FCSTD DOCUMENT  (FreeCAD 0.19R)
Label: aileron_right_assembly
License: All rights reserved
LicenseURL: http://en.wikipedia.org/wiki/All_rights_reserved
objects: App::Link×3, App::DocumentObjectGroup×2, PartDesign::CoordinateSystem×1, App::FeaturePython×1, App::Part×1
note: 1 computed .brp shape members not serialized (recipe doc carries the construction recipe); baked Part::Feature solids carry a one-line shape summary decoded from their .brp
EXTERNAL_REF file=aileron_right_part.FCStd obj=LCS_Origin
EXTERNAL_REF file=aileron_right_part.FCStd obj=Model
EXTERNAL_REF file=aileron_right_part.FCStd obj=LCS_2
EXTERNAL_REF file=attach_aileron_part.FCStd obj=LCS_1
EXTERNAL_REF file=attach_aileron_part.FCStd obj=Model
EXTERNAL_REF file=aileron_right_part.FCStd obj=LCS_1
EXTERNAL_REF file=motor_holder_aileron_part.FCStd obj=LCS_1
EXTERNAL_REF file=motor_holder_aileron_part.FCStd obj=Model

FEATURE [App::DocumentObjectGroup] Parts
FEATURE [PartDesign::CoordinateSystem] LCS_Origin
  AttacherType = Attacher::AttachEngine3D
  MapMode = 2
  Support = -> [X_Axis]
FEATURE [App::DocumentObjectGroup] Constraints
FEATURE [App::FeaturePython] Variables  # WARN: FeaturePython — macro-defined, semantics opaque (R4)
FEATURE [App::Link] aileron_right_part
  AssemblyType = Asm4EE
  AttachedBy = #LCS_Origin
  AttachedTo = Parent Assembly#LCS_Origin
  LinkedObject = -> <external aileron_right_part.FCStd>#Model
  expr: Placement = LCS_Origin.Placement * AttachmentOffset * aileron_right_part#LCS_Origin.Placement ^ -1
FEATURE [App::Link] attach_aileron_part
  AssemblyType = Asm4EE
  AttachedBy = #LCS_1
  AttachedTo = aileron_right_part#LCS_2
  AttachmentOffset = pos=(0,0,0.2) rot=(0.707107,-0.707107,0;3.14159rad)
  LinkPlacement = pos=(0,22,2.5) rot=(1,0,0;1.5708rad)
  LinkedObject = -> <external attach_aileron_part.FCStd>#Model
  Placement = pos=(0,22,2.5) rot=(1,0,0;1.5708rad)
  expr: Placement = aileron_right_part.Placement * aileron_right_part#LCS_2.Placement * AttachmentOffset * attach_aileron_part#LCS_1.Placement ^ -1
FEATURE [App::Link] motor_holder_aileron_part
  AssemblyType = Asm4EE
  AttachedBy = #LCS_1
  AttachedTo = aileron_right_part#LCS_1
  AttachmentOffset = pos=(-0.1,-0.1,-0.1) rot=(0,0,1;0rad)
  LinkPlacement = pos=(0,-2,2.5) rot=(-1,0,0;1.5708rad)
  LinkedObject = -> <external motor_holder_aileron_part.FCStd>#Model
  Placement = pos=(0,-2,2.5) rot=(-1,0,0;1.5708rad)
  expr: Placement = aileron_right_part.Placement * aileron_right_part#LCS_1.Placement * AttachmentOffset * motor_holder_aileron_part#LCS_1.Placement ^ -1
FEATURE [App::Part] Model
  Configuration = 0
  Group = -> [LCS_Origin,Constraints,Variables,aileron_right_part,attach_aileron_part,motor_holder_aileron_part]
  Origin = -> Origin
  Type = Assembly4 Model

RESOLVED EXTERNAL PARTS (link-assembly join: the EXTERNAL_REF files above that resolve inside this repo's crawl, each included once):
---- part aileron_right_part.FCStd = doc fcstd_d629c37d68a0 ----
FCSTD DOCUMENT  (FreeCAD 0.19R)
Label: aileron_right_part
License: All rights reserved
LicenseURL: http://en.wikipedia.org/wiki/All_rights_reserved
objects: Sketcher::SketchObject×8, PartDesign::Pocket×6, PartDesign::CoordinateSystem×4, App::DocumentObjectGroup×2, PartDesign::Pad×2, App::FeaturePython×1, PartDesign::Fillet×1, PartDesign::Body×1, App::Part×1
note: 31 computed .brp shape members not serialized (recipe doc carries the construction recipe); baked Part::Feature solids carry a one-line shape summary decoded from their .brp

FEATURE [App::DocumentObjectGroup] Parts
FEATURE [PartDesign::CoordinateSystem] LCS_Origin
  AttacherType = Attacher::AttachEngine3D
  MapMode = 2
  Support = -> [X_Axis]
FEATURE [App::DocumentObjectGroup] Constraints
FEATURE [App::FeaturePython] Variables  # WARN: FeaturePython — macro-defined, semantics opaque (R4)
FEATURE [PartDesign::CoordinateSystem] LCS_0
  AttacherType = Attacher::AttachEngine3D
  MapMode = 2
  Support = -> [X_Axis001]
FEATURE [Sketcher::SketchObject] Sketch
  FullyConstrained = false
  MapMode = 5
  Support = -> [XY_Plane001]
  sketch-geometry (5):
    g0: LineSegment StartX=-85 StartY=14 StartZ=0 EndX=85 EndY=14 EndZ=0
    g1: LineSegment StartX=85 StartY=14 StartZ=0 EndX=78.5357 EndY=-14 EndZ=0
    g2: LineSegment StartX=78.5357 StartY=-14 StartZ=0 EndX=-91.4643 EndY=-14 EndZ=0
    g3: LineSegment StartX=-91.4643 StartY=-14 StartZ=0 EndX=-85 EndY=14 EndZ=0
    g4: LineSegment StartX=-45.9438 StartY=14 StartZ=0 EndX=-45.9438 EndY=-14 EndZ=0
  constraints (13):
    c: Coincident(g0,g1)
    c: Coincident(g1,g2)
    c: Coincident(g2,g3)
    c: Coincident(g3,g0)
    c: Horizontal(g2)
    c: DistanceX(g0,g0) = 170
    c: Angle(g3,g0) = 1.79769
    c: Angle(g1,g2) = 1.79769
    c: PointOnObject(g4,g0)
    c: PointOnObject(g4,g2)
    c: DistanceY(g4,g4) = 28
    c: Symmetric(g4,g4,g-1)
    c: Symmetric(g0,g0,g-2)
FEATURE [PartDesign::Pad] Pad
  Direction = (1,1,1)
  Length = 5
  Length2 = 100
  Profile = -> Sketch
  Type = 0
FEATURE [Sketcher::SketchObject] Sketch001
  FullyConstrained = true
  MapMode = 5
  Placement = pos=(0,0,5) rot=(0,0,1;0rad)
  Support = -> [Pad]
  sketch-geometry (4):
    g0: LineSegment StartX=-14.5 StartY=2 StartZ=0 EndX=14.5 EndY=2 EndZ=0
    g1: LineSegment StartX=14.5 StartY=2 StartZ=0 EndX=14.5 EndY=-14 EndZ=0
    g2: LineSegment StartX=14.5 StartY=-14 StartZ=0 EndX=-14.5 EndY=-14 EndZ=0
    g3: LineSegment StartX=-14.5 StartY=-14 StartZ=0 EndX=-14.5 EndY=2 EndZ=0
  constraints (11):
    c: Coincident(g0,g1)
    c: Coincident(g1,g2)
    c: Coincident(g2,g3)
    c: Coincident(g3,g0)
    c: Horizontal(g2)
    c: Vertical(g1)
    c: Vertical(g3)
    c: DistanceY(g1,g1) = 16
    c: DistanceX(g2,g2) = 29
    c: DistanceY(g-1,g0) = 2
    c: Symmetric(g0,g0,g-2)
FEATURE [PartDesign::Pocket] Pocket
  BaseFeature = -> Pad
  Length = 5
  Length2 = 100
  Profile = -> Sketch001
  Type = 0
FEATURE [Sketcher::SketchObject] Sketch002
  FullyConstrained = true
  MapMode = 5
  Placement = pos=(0,2,0) rot=(1,0,0;1.5708rad)
  Support = -> [Pocket]
  sketch-geometry (4):
    g0: LineSegment StartX=-14.5 StartY=3.6 StartZ=0 EndX=14.5 EndY=3.6 EndZ=0
    g1: LineSegment StartX=14.5 StartY=3.6 StartZ=0 EndX=14.5 EndY=1.4 EndZ=0
    g2: LineSegment StartX=14.5 StartY=1.4 StartZ=0 EndX=-14.5 EndY=1.4 EndZ=0
    g3: LineSegment StartX=-14.5 StartY=1.4 StartZ=0 EndX=-14.5 EndY=3.6 EndZ=0
  constraints (11):
    c: Coincident(g0,g1)
    c: Coincident(g1,g2)
    c: Coincident(g2,g3)
    c: Coincident(g3,g0)
    c: Horizontal(g2)
    c: Vertical(g1)
    c: Vertical(g3)
    c: DistanceX(g0,g0) = 29
    c: DistanceY(g1,g1) = 2.2
    c: Symmetric(g0,g0,g-2)
    c: DistanceY(g-1,g1) = 1.4
FEATURE [PartDesign::Pocket] Pocket001
  BaseFeature = -> Pocket
  Length = 2.1
  Length2 = 100
  Profile = -> Sketch002
  Type = 0
FEATURE [Sketcher::SketchObject] Sketch004
  FullyConstrained = false
  MapMode = 5
  Placement = pos=(-14.5,0,0) rot=(0.57735,0.57735,0.57735;2.0944rad)
  Support = -> [Pocket001]
  sketch-geometry (3):
    g0: LineSegment StartX=-14 StartY=5 StartZ=0 EndX=2 EndY=5 EndZ=0
    g1: LineSegment StartX=2 StartY=5 StartZ=0 EndX=-14 EndY=3 EndZ=0
    g2: LineSegment StartX=-14 StartY=3 StartZ=0 EndX=-14 EndY=5 EndZ=0
  constraints (7):
    c: Coincident(g1,g2)
    c: Horizontal(g0)
    c: Vertical(g2)
    c: DistanceX(g0,g0) = 16
    c: DistanceY(g2,g2) = 2
    c: DistanceX(g-2,g1) = -14
    c: DistanceY(g-1,g0) = 5
FEATURE [PartDesign::Pocket] Pocket002
  BaseFeature = -> Pocket001
  Length = 100
  Length2 = 100
  Profile = -> Sketch004
  Type = 0
FEATURE [Sketcher::SketchObject] Sketch005
  FullyConstrained = true
  MapMode = 5
  Placement = pos=(14.5,0,0) rot=(0.57735,-0.57735,-0.57735;2.0944rad)
  Support = -> [Pocket002]
  sketch-geometry (3):
    g0: LineSegment StartX=-2 StartY=5 StartZ=0 EndX=14 EndY=5 EndZ=0
    g1: LineSegment StartX=14 StartY=5 StartZ=0 EndX=14 EndY=3 EndZ=0
    g2: LineSegment StartX=14 StartY=3 StartZ=0 EndX=-2 EndY=5 EndZ=0
  constraints (9):
    c: Coincident(g0,g1)
    c: Coincident(g1,g2)
    c: Horizontal(g0)
    c: Vertical(g1)
    c: Coincident(g2,g0)
    c: DistanceX(g0,g0) = 16
    c: DistanceY(g1,g1) = 2
    c: DistanceX(g-2,g0) = 14
    c: DistanceY(g-1,g0) = 5
FEATURE [PartDesign::Pocket] Pocket003
  BaseFeature = -> Pocket002
  Length = 100
  Length2 = 100
  Profile = -> Sketch005
  Type = 0
FEATURE [Sketcher::SketchObject] Sketch006
  FullyConstrained = true
  MapMode = 5
  Placement = pos=(0,14,0) rot=(0,0.707107,0.707107;3.14159rad)
  Support = -> [Pocket003]
  sketch-geometry (12):
    g0: LineSegment StartX=82 StartY=5 StartZ=0 EndX=85 EndY=5 EndZ=0
    g1: LineSegment StartX=85 StartY=5 StartZ=0 EndX=85 EndY=0 EndZ=0
    g2: LineSegment StartX=85 StartY=0 StartZ=0 EndX=82 EndY=0 EndZ=0
    g3: LineSegment StartX=82 StartY=0 StartZ=0 EndX=82 EndY=5 EndZ=0
    g4: LineSegment StartX=-85 StartY=5 StartZ=0 EndX=-82 EndY=5 EndZ=0
    g5: LineSegment StartX=-82 StartY=5 StartZ=0 EndX=-82 EndY=0 EndZ=0
    g6: LineSegment StartX=-82 StartY=0 StartZ=0 EndX=-85 EndY=0 EndZ=0
    g7: LineSegment StartX=-85 StartY=0 StartZ=0 EndX=-85 EndY=5 EndZ=0
    g8: LineSegment StartX=-3 StartY=5 StartZ=0 EndX=3 EndY=5 EndZ=0
    g9: LineSegment StartX=3 StartY=5 StartZ=0 EndX=3 EndY=0 EndZ=0
    g10: LineSegment StartX=3 StartY=0 StartZ=0 EndX=-3 EndY=0 EndZ=0
    g11: LineSegment StartX=-3 StartY=0 StartZ=0 EndX=-3 EndY=5 EndZ=0
  constraints (35):
    c: Coincident(g0,g1)
    c: Coincident(g1,g2)
    c: Coincident(g2,g3)
    c: Coincident(g3,g0)
    c: Horizontal(g0)
    c: Horizontal(g2)
    c: Vertical(g1)
    c: Vertical(g3)
    c: DistanceY(g1,g1) = 5
    c: DistanceX(g2,g2) = 3
    c: PointOnObject(g1,g-1)
    c: DistanceX(g-1,g0) = 85
    c: Coincident(g4,g5)
    c: Coincident(g5,g6)
    c: Coincident(g6,g7)
    c: Coincident(g7,g4)
    c: Horizontal(g4)
    c: Horizontal(g6)
    c: Vertical(g5)
    c: Vertical(g7)
    c: DistanceX(g4,g4) = 3
    c: DistanceY(g5,g5) = 5
    c: PointOnObject(g6,g-1)
    c: DistanceX(g-2,g4) = -85
    c: Coincident(g8,g9)
    c: Coincident(g9,g10)
    c: Coincident(g10,g11)
    c: Coincident(g11,g8)
    c: Horizontal(g10)
    c: Vertical(g9)
    c: Vertical(g11)
    c: DistanceY(g9,g9) = 5
    c: DistanceX(g10,g10) = 6
    c: PointOnObject(g9,g-1)
    c: Symmetric(g8,g8,g-2)
FEATURE [PartDesign::Pad] Pad001
  BaseFeature = -> Pocket003
  Direction = (1,1,1)
  Length = 5.5
  Length2 = 100
  Profile = -> Sketch006
  Type = 0
FEATURE [Sketcher::SketchObject] Sketch008
  FullyConstrained = true
  MapMode = 5
  Placement = pos=(0,0,5) rot=(0,0,1;0rad)
  Support = -> [Pocket001]
  sketch-geometry (4):
    g0: LineSegment StartX=-42.2 StartY=10 StartZ=0 EndX=-40 EndY=10 EndZ=0
    g1: LineSegment StartX=-40 StartY=10 StartZ=0 EndX=-40 EndY=4.3 EndZ=0
    g2: LineSegment StartX=-40 StartY=4.3 StartZ=0 EndX=-42.2 EndY=4.3 EndZ=0
    g3: LineSegment StartX=-42.2 StartY=4.3 StartZ=0 EndX=-42.2 EndY=10 EndZ=0
  constraints (12):
    c: Coincident(g0,g1)
    c: Coincident(g1,g2)
    c: Coincident(g2,g3)
    c: Coincident(g3,g0)
    c: Horizontal(g0)
    c: Horizontal(g2)
    c: Vertical(g1)
    c: Vertical(g3)
    c: DistanceY(g3,g3) = 5.7
    c: DistanceX(g2,g2) = 2.2
    c: DistanceY(g-1,g0) = 10
    c: DistanceX(g-2,g0) = -40
FEATURE [PartDesign::Pocket] Pocket005
  BaseFeature = -> Pad001
  Length = 5
  Length2 = 100
  Profile = -> Sketch008
  Type = 0
FEATURE [PartDesign::CoordinateSystem] LCS_1
  AttacherType = Attacher::AttachEngine3D
  MapMode = 7
  Placement = pos=(-14.5,4.1,1.4) rot=(0,1,0;3.14159rad)
  Support = -> [Pocket001]
FEATURE [PartDesign::CoordinateSystem] LCS_2
  AttacherType = Attacher::AttachEngine3D
  MapMode = 11
  Placement = pos=(82,17,2.5) rot=(0,-1,0;1.5708rad)
FEATURE [Sketcher::SketchObject] Sketch009
  FullyConstrained = false
  MapMode = 5
  Placement = pos=(85,0,0) rot=(0.57735,0.57735,0.57735;2.0944rad)
  Support = -> [Pocket005]
  sketch-geometry (3):
    g0: LineSegment StartX=17 StartY=13.2845 StartZ=0 EndX=17 EndY=-7.92734 EndZ=0
    g1: LineSegment StartX=-4.64328 StartY=2.5 StartZ=0 EndX=33.4576 EndY=2.5 EndZ=0
    g2: Circle CenterX=17 CenterY=2.5 CenterZ=0 NormalX=0 NormalY=0 NormalZ=1 AngleXU=0 Radius=0.75
  constraints (7):
    c: Vertical(g0)
    c: DistanceX(g-2,g0) = 17
    c: Horizontal(g1)
    c: DistanceY(g-1,g1) = 2.5
    c: PointOnObject(g2,g0)
    c: Diameter(g2) = 1.5
    c: PointOnObject(g2,g1)
FEATURE [PartDesign::Pocket] Pocket006
  BaseFeature = -> Pocket005
  Length = 200
  Length2 = 100
  Profile = -> Sketch009
  Type = 0
FEATURE [PartDesign::Fillet] Fillet
  Base = -> Pocket006 [Edge83,Edge66,Edge74,Edge55,Edge80,Edge47]
  BaseFeature = -> Pocket006
  Radius = 2.49
  SupportTransform = false
FEATURE [PartDesign::Body] Body
  Group = -> [LCS_0,Sketch,Pad,Sketch001,Pocket,Sketch002,Pocket001,Sketch004,Pocket002,Sketch005,Pocket003,Sketch006,Pad001,Sketch008,Pocket005,Sketch009,Pocket006,Fillet]
  Origin = -> Origin001
  Tip = -> Fillet
FEATURE [App::Part] Model
  Configuration = 0
  Group = -> [LCS_Origin,Constraints,Variables,Body,LCS_1,LCS_2]
  Origin = -> Origin
  Type = Assembly4 Model
---- part attach_aileron_part.FCStd = doc fcstd_dc8632fcb261 ----
FCSTD DOCUMENT  (FreeCAD 0.19R)
Label: attach_aileron_part
License: All rights reserved
LicenseURL: http://en.wikipedia.org/wiki/All_rights_reserved
objects: Sketcher::SketchObject×4, PartDesign::Pad×3, App::DocumentObjectGroup×2, PartDesign::CoordinateSystem×2, App::FeaturePython×1, PartDesign::Fillet×1, PartDesign::Pocket×1, PartDesign::Body×1, App::Part×1
note: 17 computed .brp shape members not serialized (recipe doc carries the construction recipe); baked Part::Feature solids carry a one-line shape summary decoded from their .brp

FEATURE [App::DocumentObjectGroup] Parts
FEATURE [PartDesign::CoordinateSystem] LCS_Origin
  AttacherType = Attacher::AttachEngine3D
  MapMode = 2
  Support = -> [X_Axis]
FEATURE [App::DocumentObjectGroup] Constraints
FEATURE [App::FeaturePython] Variables  # WARN: FeaturePython — macro-defined, semantics opaque (R4)
FEATURE [Sketcher::SketchObject] Sketch
  FullyConstrained = true
  MapMode = 5
  Support = -> [XY_Plane001]
  sketch-geometry (4):
    g0: LineSegment StartX=-85 StartY=2.5 StartZ=0 EndX=85 EndY=2.5 EndZ=0
    g1: LineSegment StartX=85 StartY=2.5 StartZ=0 EndX=85 EndY=-2.5 EndZ=0
    g2: LineSegment StartX=85 StartY=-2.5 StartZ=0 EndX=-85 EndY=-2.5 EndZ=0
    g3: LineSegment StartX=-85 StartY=-2.5 StartZ=0 EndX=-85 EndY=2.5 EndZ=0
  constraints (10):
    c: Coincident(g0,g1)
    c: Coincident(g1,g2)
    c: Coincident(g2,g3)
    c: Coincident(g3,g0)
    c: Horizontal(g2)
    c: Vertical(g3)
    c: DistanceX(g0,g0) = 170
    c: DistanceY(g3,g3) = 5
    c: Symmetric(g0,g0,g-2)
    c: Symmetric(g0,g1,g-1)
FEATURE [PartDesign::Pad] Pad
  Direction = (1,1,1)
  Length = 2
  Length2 = 100
  Profile = -> Sketch
  Type = 0
FEATURE [Sketcher::SketchObject] Sketch001
  FullyConstrained = true
  MapMode = 5
  Placement = pos=(0,0,2) rot=(0,0,1;0rad)
  Support = -> [Pad]
  sketch-geometry (16):
    g0: LineSegment StartX=-81.8 StartY=2.5 StartZ=0 EndX=-78.8 EndY=2.5 EndZ=0
    g1: LineSegment StartX=-78.8 StartY=2.5 StartZ=0 EndX=-78.8 EndY=-2.5 EndZ=0
    g2: LineSegment StartX=-78.8 StartY=-2.5 StartZ=0 EndX=-81.8 EndY=-2.5 EndZ=0
    g3: LineSegment StartX=-81.8 StartY=-2.5 StartZ=0 EndX=-81.8 EndY=2.5 EndZ=0
    g4: LineSegment StartX=78.8 StartY=2.5 StartZ=0 EndX=81.8 EndY=2.5 EndZ=0
    g5: LineSegment StartX=81.8 StartY=2.5 StartZ=0 EndX=81.8 EndY=-2.5 EndZ=0
    g6: LineSegment StartX=81.8 StartY=-2.5 StartZ=0 EndX=78.8 EndY=-2.5 EndZ=0
    g7: LineSegment StartX=78.8 StartY=-2.5 StartZ=0 EndX=78.8 EndY=2.5 EndZ=0
    g8: LineSegment StartX=-6.2 StartY=2.5 StartZ=0 EndX=-3.2 EndY=2.5 EndZ=0
    g9: LineSegment StartX=-3.2 StartY=2.5 StartZ=0 EndX=-3.2 EndY=-2.5 EndZ=0
    g10: LineSegment StartX=-3.2 StartY=-2.5 StartZ=0 EndX=-6.2 EndY=-2.5 EndZ=0
    g11: LineSegment StartX=-6.2 StartY=-2.5 StartZ=0 EndX=-6.2 EndY=2.5 EndZ=0
    g12: LineSegment StartX=3.2 StartY=2.5 StartZ=0 EndX=6.2 EndY=2.5 EndZ=0
    g13: LineSegment StartX=6.2 StartY=2.5 StartZ=0 EndX=6.2 EndY=-2.5 EndZ=0
    g14: LineSegment StartX=6.2 StartY=-2.5 StartZ=0 EndX=3.2 EndY=-2.5 EndZ=0
    g15: LineSegment StartX=3.2 StartY=-2.5 StartZ=0 EndX=3.2 EndY=2.5 EndZ=0
  constraints (44):
    c: Coincident(g0,g1)
    c: Coincident(g1,g2)
    c: Coincident(g2,g3)
    c: Coincident(g3,g0)
    c: Horizontal(g0)
    c: Horizontal(g2)
    c: Vertical(g3)
    c: DistanceY(g3,g3) = 5
    c: DistanceX(g2,g2) = 3
    c: Symmetric(g1,g0,g-1)
    c: DistanceX(g-2,g0) = -81.8
    c: Coincident(g4,g5)
    c: Coincident(g5,g6)
    c: Coincident(g6,g7)
    c: Coincident(g7,g4)
    c: Horizontal(g4)
    c: Horizontal(g6)
    c: Vertical(g5)
    c: DistanceY(g7,g7) = 5
    c: DistanceX(g6,g6) = 3
    c: Symmetric(g6,g4,g-1)
    c: DistanceX(g-2,g4) = 81.8
    c: Coincident(g8,g9)
    c: Coincident(g9,g10)
    c: Coincident(g10,g11)
    c: Coincident(g11,g8)
    c: Horizontal(g8)
    c: Horizontal(g10)
    c: Vertical(g11)
    c: DistanceY(g11,g11) = 5
    c: DistanceX(g10,g10) = 3
    c: Symmetric(g9,g8,g-1)
    c: DistanceX(g-2,g8) = -3.2
    c: Coincident(g12,g13)
    c: Coincident(g13,g14)
    c: Coincident(g14,g15)
    c: Coincident(g15,g12)
    c: Horizontal(g12)
    c: Horizontal(g14)
    c: Vertical(g15)
    c: DistanceY(g15,g15) = 5
    c: DistanceX(g14,g14) = 3
    c: Symmetric(g13,g12,g-1)
    c: DistanceX(g-2,g12) = 3.2
FEATURE [PartDesign::Pad] Pad001
  BaseFeature = -> Pad
  Direction = (1,1,1)
  Length = 5.5
  Length2 = 100
  Profile = -> Sketch001
  Type = 0
FEATURE [PartDesign::Fillet] Fillet
  Base = -> Pad001 [Edge53,Edge58,Edge63,Edge68,Edge42,Edge36,Edge30,Edge24]
  BaseFeature = -> Pad001
  Radius = 2.49
  SupportTransform = false
FEATURE [Sketcher::SketchObject] Sketch002
  FullyConstrained = false
  MapMode = 5
  Placement = pos=(81.8,0,0) rot=(0.57735,0.57735,0.57735;2.0944rad)
  Support = -> [Fillet]
  sketch-geometry (2):
    g0: LineSegment StartX=-7.13275 StartY=5 StartZ=0 EndX=6.93936 EndY=5 EndZ=0
    g1: Circle CenterX=0 CenterY=5 CenterZ=0 NormalX=0 NormalY=0 NormalZ=1 AngleXU=0 Radius=0.75
  constraints (5):
    c: Horizontal(g0)
    c: DistanceY(g-1,g0) = 5
    c: PointOnObject(g1,g-2)
    c: PointOnObject(g1,g0)
    c: Diameter(g1) = 1.5
FEATURE [PartDesign::Pocket] Pocket
  BaseFeature = -> Fillet
  Length = 200
  Length2 = 100
  Profile = -> Sketch002
  Type = 0
FEATURE [Sketcher::SketchObject] Sketch003
  FullyConstrained = true
  MapMode = 5
  Placement = pos=(0,0,0) rot=(1,0,0;3.14159rad)
  Support = -> [Pocket]
  sketch-geometry (12):
    g0: LineSegment StartX=-81.9 StartY=2.5 StartZ=0 EndX=-78.9 EndY=2.5 EndZ=0
    g1: LineSegment StartX=-78.9 StartY=2.5 StartZ=0 EndX=-78.9 EndY=-2.5 EndZ=0
    g2: LineSegment StartX=-78.9 StartY=-2.5 StartZ=0 EndX=-81.9 EndY=-2.5 EndZ=0
    g3: LineSegment StartX=-81.9 StartY=-2.5 StartZ=0 EndX=-81.9 EndY=2.5 EndZ=0
    g4: LineSegment StartX=-3 StartY=2.5 StartZ=0 EndX=3 EndY=2.5 EndZ=0
    g5: LineSegment StartX=3 StartY=2.5 StartZ=0 EndX=3 EndY=-2.5 EndZ=0
    g6: LineSegment StartX=3 StartY=-2.5 StartZ=0 EndX=-3 EndY=-2.5 EndZ=0
    g7: LineSegment StartX=-3 StartY=-2.5 StartZ=0 EndX=-3 EndY=2.5 EndZ=0
    g8: LineSegment StartX=78.9 StartY=2.5 StartZ=0 EndX=81.9 EndY=2.5 EndZ=0
    g9: LineSegment StartX=81.9 StartY=2.5 StartZ=0 EndX=81.9 EndY=-2.5 EndZ=0
    g10: LineSegment StartX=81.9 StartY=-2.5 StartZ=0 EndX=78.9 EndY=-2.5 EndZ=0
    g11: LineSegment StartX=78.9 StartY=-2.5 StartZ=0 EndX=78.9 EndY=2.5 EndZ=0
  constraints (32):
    c: Coincident(g0,g1)
    c: Coincident(g1,g2)
    c: Coincident(g2,g3)
    c: Coincident(g3,g0)
    c: Horizontal(g0)
    c: Horizontal(g2)
    c: Vertical(g1)
    c: DistanceY(g3,g3) = 5
    c: DistanceX(g2,g2) = 3
    c: Symmetric(g0,g2,g-1)
    c: DistanceX(g-2,g0) = -81.9
    c: Coincident(g4,g5)
    c: Coincident(g5,g6)
    c: Coincident(g6,g7)
    c: Coincident(g7,g4)
    c: Horizontal(g6)
    c: Vertical(g7)
    c: DistanceY(g7,g7) = 5
    c: DistanceX(g6,g6) = 6
    c: Symmetric(g4,g4,g-2)
    c: Symmetric(g5,g4,g-1)
    c: Coincident(g8,g9)
    c: Coincident(g9,g10)
    c: Coincident(g10,g11)
    c: Coincident(g11,g8)
    c: Horizontal(g8)
    c: Horizontal(g10)
    c: Vertical(g11)
    c: DistanceY(g11,g11) = 5
    c: DistanceX(g10,g10) = 3
    c: Symmetric(g9,g8,g-1)
    c: DistanceX(g-2,g8) = 81.9
FEATURE [PartDesign::Pad] Pad002
  BaseFeature = -> Pocket
  Direction = (1,1,1)
  Length = 10
  Length2 = 100
  Profile = -> Sketch003
  Type = 0
FEATURE [PartDesign::Body] Body
  Group = -> [Sketch,Pad,Sketch001,Pad001,Fillet,Sketch002,Pocket,Sketch003,Pad002]
  Origin = -> Origin001
  Tip = -> Pad002
FEATURE [PartDesign::CoordinateSystem] LCS_1
  AttacherType = Attacher::AttachEngine3D
  MapMode = 11
  Placement = pos=(81.8,0,5) rot=(0.707107,0,0.707107;3.14159rad)
  Support = -> [Pad002]
FEATURE [App::Part] Model
  Configuration = 0
  Group = -> [LCS_Origin,Constraints,Variables,Body,LCS_1]
  Origin = -> Origin
  Type = Assembly4 Model
---- part motor_holder_aileron_part.FCStd = doc fcstd_5347285232eb ----
FCSTD DOCUMENT  (FreeCAD 0.19R)
Label: motor_holder_aileron_part
License: All rights reserved
LicenseURL: http://en.wikipedia.org/wiki/All_rights_reserved
objects: Sketcher::SketchObject×4, PartDesign::Pad×3, App::DocumentObjectGroup×2, PartDesign::CoordinateSystem×2, App::FeaturePython×1, PartDesign::Pocket×1, PartDesign::Fillet×1, PartDesign::Body×1, App::Part×1
note: 17 computed .brp shape members not serialized (recipe doc carries the construction recipe); baked Part::Feature solids carry a one-line shape summary decoded from their .brp

FEATURE [App::DocumentObjectGroup] Parts
FEATURE [PartDesign::CoordinateSystem] LCS_Origin
  AttacherType = Attacher::AttachEngine3D
  MapMode = 2
  Support = -> [X_Axis]
FEATURE [App::DocumentObjectGroup] Constraints
FEATURE [App::FeaturePython] Variables  # WARN: FeaturePython — macro-defined, semantics opaque (R4)
FEATURE [Sketcher::SketchObject] Sketch004
  FullyConstrained = true
  MapMode = 5
  Placement = pos=(0,0,0) rot=(1,0,0;3.14159rad)
  sketch-geometry (4):
    g0: LineSegment StartX=-14.4 StartY=1 StartZ=0 EndX=14.4 EndY=1 EndZ=0
    g1: LineSegment StartX=14.4 StartY=1 StartZ=0 EndX=14.4 EndY=-1 EndZ=0
    g2: LineSegment StartX=14.4 StartY=-1 StartZ=0 EndX=-14.4 EndY=-1 EndZ=0
    g3: LineSegment StartX=-14.4 StartY=-1 StartZ=0 EndX=-14.4 EndY=1 EndZ=0
  constraints (10):
    c: Coincident(g0,g1)
    c: Coincident(g1,g2)
    c: Coincident(g2,g3)
    c: Coincident(g3,g0)
    c: Horizontal(g2)
    c: Vertical(g1)
    c: DistanceX(g0,g0) = 28.8
    c: DistanceY(g1,g1) = 2
    c: Symmetric(g0,g0,g-2)
    c: Symmetric(g2,g0,g-1)
FEATURE [Sketcher::SketchObject] Sketch
  FullyConstrained = false
  MapMode = 5
  Support = -> [XY_Plane001]
  sketch-geometry (7):
    g0: Circle CenterX=0 CenterY=0 CenterZ=0 NormalX=0 NormalY=0 NormalZ=1 AngleXU=0 Radius=13.5
    g1: Circle CenterX=-5.65685 CenterY=-5.65685 CenterZ=0 NormalX=0 NormalY=0 NormalZ=1 AngleXU=0 Radius=1.75
    g2: Circle CenterX=5.65685 CenterY=5.65685 CenterZ=0 NormalX=0 NormalY=0 NormalZ=1 AngleXU=0 Radius=1.75
    g3: Circle CenterX=-5.65685 CenterY=5.65685 CenterZ=0 NormalX=0 NormalY=0 NormalZ=1 AngleXU=0 Radius=1.75
    g4: Circle CenterX=5.65685 CenterY=-5.65685 CenterZ=0 NormalX=0 NormalY=0 NormalZ=1 AngleXU=0 Radius=1.75
    g5: LineSegment StartX=-16.3288 StartY=-16.3288 StartZ=0 EndX=16.5596 EndY=16.5596 EndZ=0
    g6: LineSegment StartX=-12.9244 StartY=12.9244 StartZ=0 EndX=15.1797 EndY=-15.1797 EndZ=0
  constraints (18):
    c: Coincident(g0,g-1)
    c: Diameter(g0) = 27
    c: Diameter(g1) = 3.5
    c: Diameter(g2) = 3.5
    c: Diameter(g3) = 3.5
    c: Diameter(g4) = 3.5
    c: PointOnObject(g0,g5)
    c: Angle(g5) = 0.785398
    c: PointOnObject(g0,g6)
    c: Angle(g6) = -0.785398
    c: PointOnObject(g2,g5)
    c: PointOnObject(g1,g5)
    c: PointOnObject(g4,g6)
    c: Distance(g3,g5) = 8
    c: Distance(g0,g1) = 8
    c: Distance(g0,g2) = 8
    c: PointOnObject(g3,g6)
    c: Distance(g0,g4) = 8
FEATURE [PartDesign::Pad] Pad
  Direction = (1,1,1)
  Length = 4
  Length2 = 100
  Profile = -> Sketch
  Type = 0
FEATURE [PartDesign::Pad] Pad001
  BaseFeature = -> Pad
  Direction = (1,1,1)
  Length = 6
  Length2 = 100
  Profile = -> Sketch004
  Reversed = true
  Type = 0
FEATURE [Sketcher::SketchObject] Sketch005
  FullyConstrained = true
  MapMode = 5
  Placement = pos=(0,0,0) rot=(1,0,0;3.14159rad)
  Support = -> [Pad001]
  sketch-geometry (1):
    g0: Circle CenterX=0 CenterY=0 CenterZ=0 NormalX=0 NormalY=0 NormalZ=1 AngleXU=0 Radius=4
  constraints (2):
    c: Diameter(g0) = 8
    c: Coincident(g0,g-1)
FEATURE [PartDesign::Pocket] Pocket
  BaseFeature = -> Pad001
  Length = 3
  Length2 = 100
  Profile = -> Sketch005
  Type = 0
FEATURE [PartDesign::CoordinateSystem] LCS_1
  AttacherType = Attacher::AttachEngine3D
  MapMode = 7
  Placement = pos=(-14.4,1,6) rot=(0,0.707107,0.707107;3.14159rad)
  Support = -> [Pocket]
FEATURE [Sketcher::SketchObject] Sketch006
  FullyConstrained = false
  MapMode = 5
  Placement = pos=(0,0,4) rot=(0,0,1;0rad)
  Support = -> [Pocket]
  sketch-geometry (10):
    g0: LineSegment StartX=-16.2537 StartY=-2.6 StartZ=0 EndX=18.2285 EndY=-2.6 EndZ=0
    g1: LineSegment StartX=-20.9704 StartY=2.6 StartZ=0 EndX=21.7098 EndY=2.6 EndZ=0
    g2: LineSegment StartX=-2.5 StartY=-2.6 StartZ=0 EndX=2.5 EndY=-2.6 EndZ=0
    g3: LineSegment StartX=2.5 StartY=-2.6 StartZ=0 EndX=2.5 EndY=-12.6 EndZ=0
    g4: LineSegment StartX=2.5 StartY=-12.6 StartZ=0 EndX=-2.5 EndY=-12.6 EndZ=0
    g5: LineSegment StartX=-2.5 StartY=-12.6 StartZ=0 EndX=-2.5 EndY=-2.6 EndZ=0
    g6: LineSegment StartX=-2.5 StartY=12.6 StartZ=0 EndX=2.5 EndY=12.6 EndZ=0
    g7: LineSegment StartX=2.5 StartY=12.6 StartZ=0 EndX=2.5 EndY=2.6 EndZ=0
    g8: LineSegment StartX=2.5 StartY=2.6 StartZ=0 EndX=-2.5 EndY=2.6 EndZ=0
    g9: LineSegment StartX=-2.5 StartY=2.6 StartZ=0 EndX=-2.5 EndY=12.6 EndZ=0
  constraints (26):
    c: Horizontal(g0)
    c: Horizontal(g1)
    c: DistanceY(g-1,g1) = 2.6
    c: DistanceY(g-1,g0) = -2.6
    c: Coincident(g2,g3)
    c: Coincident(g3,g4)
    c: Coincident(g4,g5)
    c: Coincident(g5,g2)
    c: Horizontal(g4)
    c: Vertical(g3)
    c: Vertical(g5)
    c: DistanceY(g5,g5) = 10
    c: DistanceX(g2,g2) = 5
    c: Symmetric(g2,g2,g-2)
    c: PointOnObject(g2,g0)
    c: Coincident(g6,g7)
    c: Coincident(g7,g8)
    c: Coincident(g8,g9)
    c: Coincident(g9,g6)
    c: Horizontal(g6)
    c: Vertical(g7)
    c: Vertical(g9)
    c: DistanceY(g9,g9) = 10
    c: DistanceX(g6,g6) = 5
    c: Symmetric(g7,g8,g-2)
    c: PointOnObject(g7,g1)
FEATURE [PartDesign::Pad] Pad002
  BaseFeature = -> Pocket
  Direction = (1,1,1)
  Length = 10
  Length2 = 100
  Profile = -> Sketch006
  Type = 0
FEATURE [PartDesign::Fillet] Fillet
  Base = -> Pad002 [Edge74,Edge63]
  BaseFeature = -> Pad002
  Radius = 9.9
  SupportTransform = false
FEATURE [PartDesign::Body] Body
  Group = -> [Sketch,Pad,Sketch004,Pad001,Sketch005,Pocket,Sketch006,Pad002,Fillet]
  Origin = -> Origin001
  Tip = -> Fillet
FEATURE [App::Part] Model
  Configuration = 0
  Group = -> [LCS_Origin,Constraints,Variables,Body,LCS_1]
  Origin = -> Origin
  Type = Assembly4 Model
